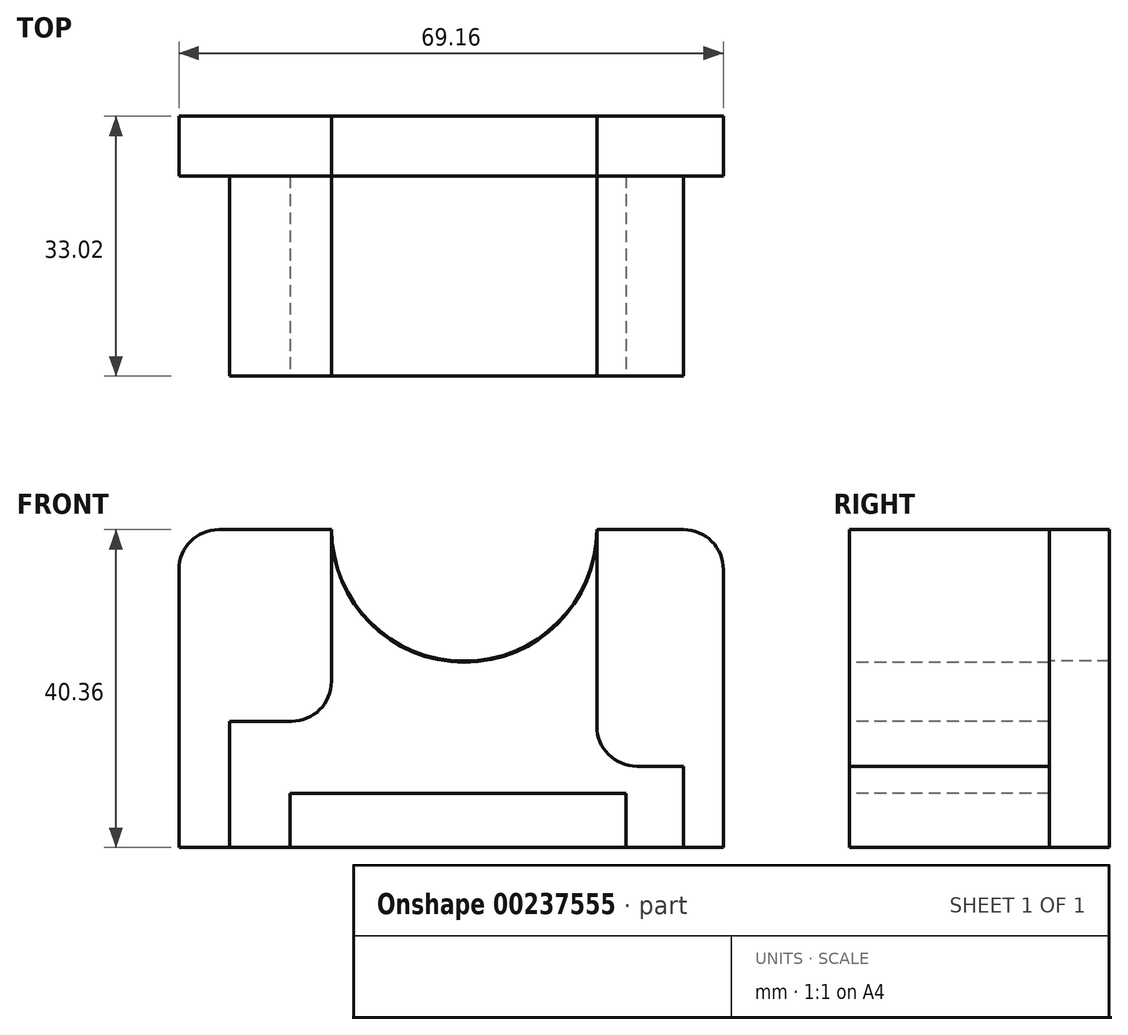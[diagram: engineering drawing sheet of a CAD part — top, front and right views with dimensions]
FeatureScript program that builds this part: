
annotation { "Feature Type Name" : "Feature", "Feature Type Description" : "" }
export const myFeature = defineFeature(function(context is Context, id is Id, definition is map)
    precondition{}
    {
        {
            var Q0;
            Q0=qCreatedBy(makeId("Front.planeOp"),FACE);
            var sketch = newSketch(context, id + "F0", { "sketchPlane" : qUnion([Q0])});
            skLineSegment(sketch, "E0.bottom", {"start": v(-34.58, 20.18) * mm, "end": v(34.58, 20.18) * mm});
            skLineSegment(sketch, "E0.top", {"start": v(-34.58, -20.18) * mm, "end": v(34.58, -20.18) * mm});
            skLineSegment(sketch, "E0.left", {"start": v(-34.58, 20.18) * mm, "end": v(-34.58, -20.18) * mm});
            skLineSegment(sketch, "E0.right", {"start": v(34.58, 20.18) * mm, "end": v(34.58, -20.18) * mm});
            skPoint(sketch, "E0.middle", {"position": v(0, 0) * mm});
            skSolve(sketch);
        }
        {
            var Q0;
            Q0=makeQuery(id+"F0.imprint","IMPRINT",FACE,{"disambiguationData":[TD([[makeQuery(id+"F0.imprint","IMPRINT",EDGE,{"derivedFrom":sQuery(id+"F0.wireOp",EDGE,"E0.bottom")}),-1.0]])]});
            extrude(context, id + "F1", {"entities" : qUnion([Q0]), "depth" : 7.62 * mm});
        }
        {
            var Q0;
            Q0=makeQuery(id+"F1.opExtrude","SWEPT_EDGE",EDGE,{"disambiguationData":[OSD([sQuery(id+"F0.wireOp",EDGE,"E0.bottom"),sQuery(id+"F0.wireOp",EDGE,"E0.left")])]});
            var Q1;
            Q1=makeQuery(id+"F1.opExtrude","SWEPT_EDGE",EDGE,{"disambiguationData":[OSD([sQuery(id+"F0.wireOp",EDGE,"E0.bottom"),sQuery(id+"F0.wireOp",EDGE,"E0.right")])]});
            fillet(context, id + "F2", {"entities" : qUnion([Q0, Q1]), "radius" : 5.08 * mm, "tangentPropagation" : true, "allowEdgeOverflow" : false});
        }
        {
            var Q0;
            Q0=makeQuery(id+"F1.opExtrude","CAP_FACE",FACE,{"disambiguationData":[OSD([sQuery(id+"F0.wireOp",EDGE,"E0.bottom"),sQuery(id+"F0.wireOp",EDGE,"E0.top"),sQuery(id+"F0.wireOp",EDGE,"E0.left"),sQuery(id+"F0.wireOp",EDGE,"E0.right")])],"isStart":false});
            var sketch = newSketch(context, id + "F3", { "sketchPlane" : qUnion([Q0])});
            skLineSegment(sketch, "E1.bottom", {"start": v(-28.14, -20.18) * mm, "end": v(29.5, -20.18) * mm});
            skLineSegment(sketch, "E1.top", {"start": v(-28.14, 20.18) * mm, "end": v(29.5, 20.18) * mm});
            skLineSegment(sketch, "E1.left", {"start": v(-28.14, -20.18) * mm, "end": v(-28.14, 20.18) * mm});
            skLineSegment(sketch, "E1.right", {"start": v(29.5, -20.18) * mm, "end": v(29.5, 20.18) * mm});
            skSolve(sketch);
        }
        {
            var Q0;
            Q0=makeQuery(id+"F3.imprint","IMPRINT",FACE,{"disambiguationData":[TD([[makeQuery(id+"F3.imprint","IMPRINT",EDGE,{"derivedFrom":sQuery(id+"F3.wireOp",EDGE,"E1.bottom")}),1.0]])]});
            extrude(context, id + "F4", {"entities" : qUnion([Q0]), "operationType" : NewBodyOperationType.ADD, "depth" : 25.4 * mm});
        }
        {
            var Q0;
            Q0=makeQuery(id+"F4.opExtrude","CAP_FACE",FACE,{"disambiguationData":[OSD([sQuery(id+"F3.wireOp",EDGE,"E1.bottom"),sQuery(id+"F3.wireOp",EDGE,"E1.top"),sQuery(id+"F3.wireOp",EDGE,"E1.left"),sQuery(id+"F3.wireOp",EDGE,"E1.right")])],"isStart":false});
            var sketch = newSketch(context, id + "F5", { "sketchPlane" : qUnion([Q0])});
            skLineSegment(sketch, "E2.bottom", {"start": v(-20.46, -20.18) * mm, "end": v(22.22, -20.18) * mm});
            skLineSegment(sketch, "E2.top", {"start": v(-20.46, -13.32) * mm, "end": v(22.22, -13.32) * mm});
            skLineSegment(sketch, "E2.left", {"start": v(-20.46, -20.18) * mm, "end": v(-20.46, -13.32) * mm});
            skLineSegment(sketch, "E2.right", {"start": v(22.22, -20.18) * mm, "end": v(22.22, -13.32) * mm});
            skLineSegment(sketch, "E3.bottom", {"start": v(-28.14, -4.18) * mm, "end": v(-15.2, -4.18) * mm});
            skLineSegment(sketch, "E3.top", {"start": v(-28.14, 20.18) * mm, "end": v(-15.2, 20.18) * mm});
            skLineSegment(sketch, "E3.left", {"start": v(-28.14, -4.18) * mm, "end": v(-28.14, 20.18) * mm});
            skLineSegment(sketch, "E3.right", {"start": v(-15.2, -4.18) * mm, "end": v(-15.2, 20.18) * mm});
            skLineSegment(sketch, "E4.bottom", {"start": v(29.5, -9.88) * mm, "end": v(18.5, -9.88) * mm});
            skLineSegment(sketch, "E4.top", {"start": v(29.5, 20.18) * mm, "end": v(18.5, 20.18) * mm});
            skLineSegment(sketch, "E4.left", {"start": v(29.5, -9.88) * mm, "end": v(29.5, 20.18) * mm});
            skLineSegment(sketch, "E4.right", {"start": v(18.5, -9.88) * mm, "end": v(18.5, 20.18) * mm});
            skArc(sketch, "E5", {"start": v(-15.2, 20.18) * mm, "mid": v(1.65, 3.33) * mm, "end": v(18.5, 20.18) * mm});
            skSolve(sketch);
        }
        {
            var Q0;
            Q0=makeQuery(id+"F5.imprint","IMPRINT",FACE,{"disambiguationData":[TD([[makeQuery(id+"F5.imprint","IMPRINT",EDGE,{"derivedFrom":sQuery(id+"F5.wireOp",EDGE,"E3.bottom")}),1.0]])]});
            var Q1;
            {var subQ0=sQuery(id+"F5.wireOp",EDGE,"E5");Q1=makeQuery(id+"F5.imprint","IMPRINT",FACE,{"disambiguationData":[TD([[makeQuery(id+"F5.imprint","IMPRINT",EDGE,{"derivedFrom":subQ0}),1.0]])]});}
            var Q2;
            Q2=makeQuery(id+"F5.imprint","IMPRINT",FACE,{"disambiguationData":[TD([[makeQuery(id+"F5.imprint","IMPRINT",EDGE,{"derivedFrom":sQuery(id+"F5.wireOp",EDGE,"E4.bottom")}),-1.0]])]});
            var Q3;
            Q3=makeQuery(id+"F5.imprint","IMPRINT",FACE,{"disambiguationData":[TD([[makeQuery(id+"F5.imprint","IMPRINT",EDGE,{"derivedFrom":sQuery(id+"F5.wireOp",EDGE,"E2.bottom")}),1.0]])]});
            extrude(context, id + "F6", {"entities" : qUnion([Q0, Q1, Q2, Q3]), "operationType" : NewBodyOperationType.REMOVE, "oppositeDirection" : true, "depth" : 25.4 * mm});
        }
        {
            var Q0;
            Q0=makeQuery(id+"F6.boolean.opBoolean","COPY",EDGE,{"derivedFrom":makeQuery(id+"F6.opExtrude","SWEPT_EDGE",EDGE,{"disambiguationData":[OSD([sQuery(id+"F5.wireOp",EDGE,"E4.bottom"),sQuery(id+"F5.wireOp",EDGE,"E4.right")])]})});
            var Q1;
            Q1=makeQuery(id+"F6.boolean.opBoolean","COPY",EDGE,{"derivedFrom":makeQuery(id+"F6.opExtrude","SWEPT_EDGE",EDGE,{"disambiguationData":[OSD([sQuery(id+"F5.wireOp",EDGE,"E3.bottom"),sQuery(id+"F5.wireOp",EDGE,"E3.right")])]})});
            fillet(context, id + "F7", {"entities" : qUnion([Q0, Q1]), "radius" : 5.08 * mm, "tangentPropagation" : true, "allowEdgeOverflow" : false});
        }
        {
            var Q0;
            Q0=makeQuery(id+"F6.boolean.opBoolean","COPY",FACE,{"derivedFrom":makeQuery(id+"F6.opExtrude","CAP_FACE",FACE,{"disambiguationData":[OSD([sQuery(id+"F3.wireOp",EDGE,"E1.top"),sQuery(id+"F5.wireOp",EDGE,"E5")])],"isStart":false})});
            var sketch = newSketch(context, id + "F8", { "sketchPlane" : qUnion([Q0])});
            skArc(sketch, "E6", {"start": v(-15.2, 20.18) * mm, "mid": v(1.65, 3.47) * mm, "end": v(18.5, 20.18) * mm});
            skSolve(sketch);
        }
        {
            var Q0;
            Q0=makeQuery(id+"F8.imprint","IMPRINT",FACE,{"disambiguationData":[TD([[makeQuery(id+"F8.imprint","IMPRINT",EDGE,{"derivedFrom":sQuery(id+"F8.wireOp",EDGE,"E6")}),1.0]])]});
            extrude(context, id + "F9", {"entities" : qUnion([Q0]), "operationType" : NewBodyOperationType.REMOVE, "oppositeDirection" : true, "depth" : 25.4 * mm});
        }
    });
